# Revit family: Lighting - Alva Wallis Wall Sconce
name_source: partatom
category: Lighting Fixtures
units: mm (PartAtom-declared; Revit-internal decimal feet)

## family parameters
Cut with Voids When Loaded = No
Host = Face
Light Source = Yes
Part Type = Normal
Room Calculation Point = No
Round Connector Dimension = Use Diameter
Shared = No

## types (4) — shared parameters
Apparent Load = 41 VA
Color Filter = 16777215
Default Elevation = 4' - 0"
Description = Indirect wall grazing luminaire for exterior/interior use
Dimming Lamp Color Temperature Shift = <None>
Emit from Line Length = 1' - 3 1/2"
Height = 0' - 5"
Lamp = LED
Lens = ALVA Lens
Manufacturer = ALVA LIGHTING
Metal = ALVA Enviro Oil-Rubbed Bronze
Photometric Web File = W8770_IESNA2002.IES
Tilt Angle = 0.00°
Top Cap = Yes
Type Comments = IP66 RATED, 120-277V INPUT,OCC SENSOR, DARK SKY, 10 YEAR LIMITED WARRANTY
URL = https://www.alvalight.com

## per-type parameters (varying)
| type | Model |
| 3000K | WALLIS 3000 M2 DB |
| 2700K | WALLIS 2700 M2 DB |
| 3500K | WALLIS 3500 M2 DB |
| 4000K | WALLIS 4000 M2 DB |

## geometry (parser evidence)
native form markers: Sweep x2
no freeform markers — native parametric forms only
